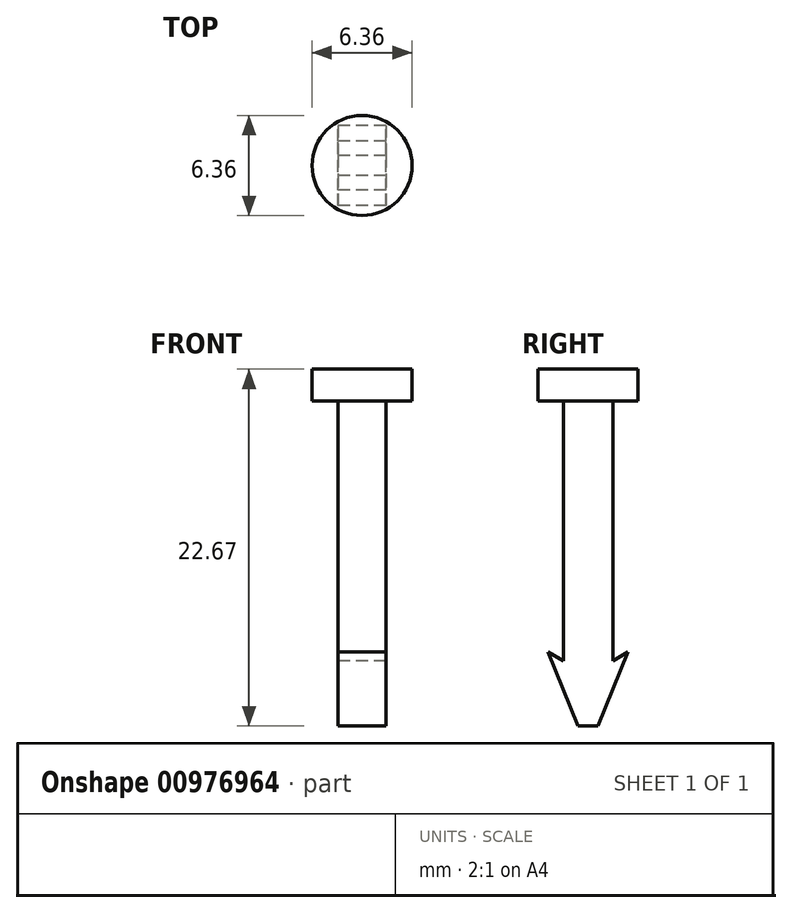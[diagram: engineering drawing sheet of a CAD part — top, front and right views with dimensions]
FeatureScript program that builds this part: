
annotation { "Feature Type Name" : "Feature", "Feature Type Description" : "" }
export const myFeature = defineFeature(function(context is Context, id is Id, definition is map)
    precondition{}
    {
        {
            var Q0;
            Q0=qCreatedBy(makeId("Top.planeOp"),FACE);
            var sketch = newSketch(context, id + "F0", { "sketchPlane" : qUnion([Q0])});
            skCircle(sketch, "E0", {"center": v(0, 0) * mm, "radius": 3.18 * mm});
            skSolve(sketch);
        }
        {
            var Q0;
            Q0 = qSketchRegion(id + "F0", true);
            extrude(context, id + "F1", {"entities" : qUnion([Q0]), "depth" : 2.03 * mm, "offsetDistance" : 25.4 * mm});
        }
        {
            var Q0;
            Q0=qCreatedBy(makeId("Right.planeOp"),FACE);
            var sketch = newSketch(context, id + "F2", { "sketchPlane" : qUnion([Q0])});
            skLineSegment(sketch, "E1", {"start": v(1.56, 0) * mm, "end": v(1.56, -16.5) * mm});
            skLineSegment(sketch, "E2", {"start": v(-1.56, -16.5) * mm, "end": v(-1.56, 0) * mm});
            skLineSegment(sketch, "E3", {"start": v(1.56, -16.5) * mm, "end": v(2.54, -15.94) * mm});
            skLineSegment(sketch, "E4", {"start": v(2.54, -15.94) * mm, "end": v(0.64, -20.64) * mm});
            skLineSegment(sketch, "E5", {"start": v(0.64, -20.64) * mm, "end": v(-0.64, -20.64) * mm});
            skLineSegment(sketch, "E6", {"start": v(-0.64, -20.64) * mm, "end": v(-2.54, -15.94) * mm});
            skLineSegment(sketch, "E7", {"start": v(-2.54, -15.94) * mm, "end": v(-1.56, -16.5) * mm});
            skPoint(sketch, "E8", {"position": v(0, -20.64) * mm});
            skLineSegment(sketch, "E9", {"start": v(-1.56, 0) * mm, "end": v(1.56, 0) * mm});
            skSolve(sketch);
        }
        {
            var Q0;
            Q0=makeQuery(id+"F2.imprint","IMPRINT",FACE,{"disambiguationData":[TD([[makeQuery(id+"F2.imprint","IMPRINT",EDGE,{"derivedFrom":sQuery(id+"F2.wireOp",EDGE,"E1")}),-1.0]])]});
            extrude(context, id + "F3", {"entities" : qUnion([Q0]), "operationType" : NewBodyOperationType.ADD, "endBound" : BoundingType.SYMMETRIC, "depth" : 3.05 * mm, "offsetDistance" : 25.4 * mm});
        }
    });
